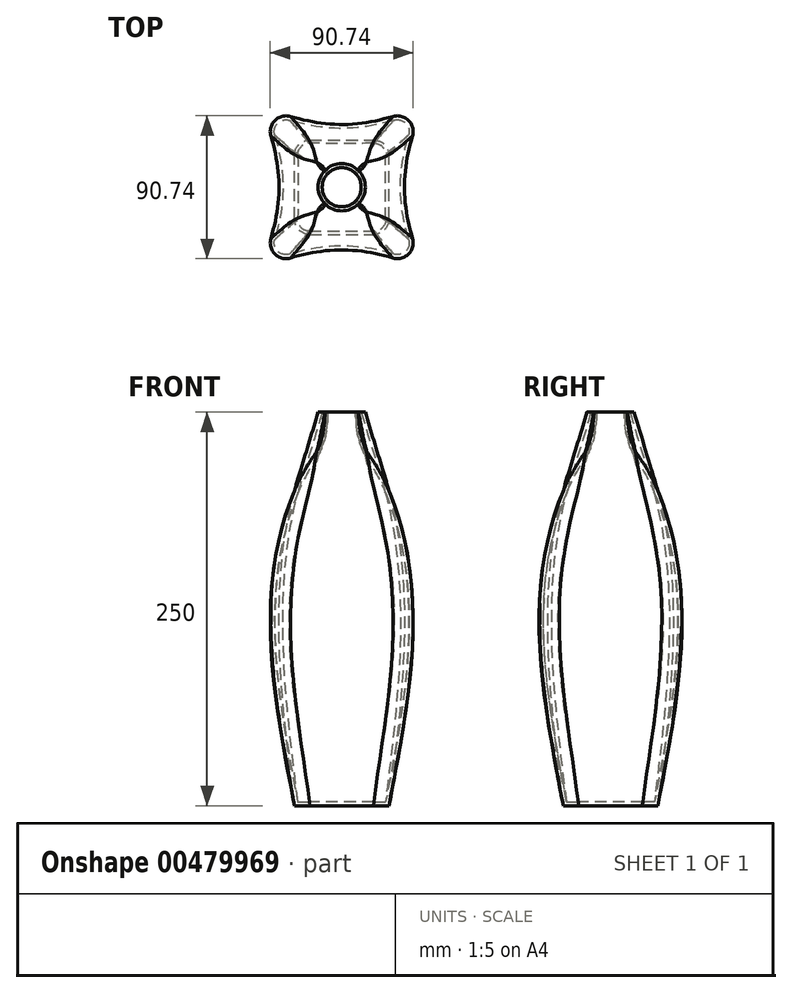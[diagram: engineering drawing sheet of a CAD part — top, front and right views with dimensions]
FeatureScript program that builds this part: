
annotation { "Feature Type Name" : "Feature", "Feature Type Description" : "" }
export const myFeature = defineFeature(function(context is Context, id is Id, definition is map)
    precondition{}
    {
        {
            var Q0;
            Q0=qCreatedBy(makeId("Top.planeOp"),FACE);
            var sketch = newSketch(context, id + "F0", { "sketchPlane" : qUnion([Q0])});
            skLineSegment(sketch, "E0.bottom", {"start": v(-30, -30) * mm, "end": v(30, -30) * mm});
            skLineSegment(sketch, "E0.top", {"start": v(-30, 30) * mm, "end": v(30, 30) * mm});
            skLineSegment(sketch, "E0.left", {"start": v(-30, -30) * mm, "end": v(-30, 30) * mm});
            skLineSegment(sketch, "E0.right", {"start": v(30, -30) * mm, "end": v(30, 30) * mm});
            skPoint(sketch, "E0.middle", {"position": v(0, 0) * mm});
            skSolve(sketch);
        }
        {
            var Q0;
            Q0=makeQuery(id+"F0.imprint","IMPRINT",FACE,{"disambiguationData":[TD([[makeQuery(id+"F0.imprint","IMPRINT",EDGE,{"derivedFrom":sQuery(id+"F0.wireOp",EDGE,"E0.bottom")}),1.0]])]});
            cPlane(context, id + "F1", {"entities" : qUnion([Q0]), "cplaneType" : CPlaneType.OFFSET, "offset" : 200 * mm, "width" : 150 * mm, "height" : 150 * mm});
        }
        {
            var Q0;
            Q0=qCreatedBy(id+"F1.planeOp",FACE);
            var sketch = newSketch(context, id + "F2", { "sketchPlane" : qUnion([Q0])});
            skLineSegment(sketch, "E1.bottom", {"start": v(30, -30) * mm, "end": v(-30, -30) * mm});
            skLineSegment(sketch, "E1.top", {"start": v(30, 30) * mm, "end": v(-30, 30) * mm});
            skLineSegment(sketch, "E1.left", {"start": v(30, -30) * mm, "end": v(30, 30) * mm});
            skLineSegment(sketch, "E1.right", {"start": v(-30, -30) * mm, "end": v(-30, 30) * mm});
            skPoint(sketch, "E1.middle", {"position": v(0, 0) * mm});
            skSolve(sketch);
        }
        {
            var Q0;
            Q0=qCreatedBy(id+"F1.planeOp",FACE);
            cPlane(context, id + "F3", {"entities" : qUnion([Q0]), "cplaneType" : CPlaneType.OFFSET, "offset" : 25 * mm, "width" : 150 * mm, "height" : 150 * mm});
        }
        {
            var Q0;
            Q0=qCreatedBy(id+"F3.planeOp",FACE);
            var sketch = newSketch(context, id + "F4", { "sketchPlane" : qUnion([Q0])});
            skPoint(sketch, "E2.middle", {"position": v(0, 0) * mm});
            skPoint(sketch, "E2.right.end.orphan", {"position": v(-32.39, 32.39) * mm});
            skPoint(sketch, "E2.bottom.end.orphan", {"position": v(-32.39, -32.39) * mm});
            skPoint(sketch, "E2.left.end.orphan", {"position": v(32.39, 32.39) * mm});
            skPoint(sketch, "E2.left.start.orphan", {"position": v(32.39, -32.39) * mm});
            skCircle(sketch, "E3", {"center": v(0, 0) * mm, "radius": 22.5 * mm});
            skSolve(sketch);
        }
        {
            var Q0;
            Q0=qCreatedBy(id+"F3.planeOp",FACE);
            cPlane(context, id + "F5", {"entities" : qUnion([Q0]), "cplaneType" : CPlaneType.OFFSET, "offset" : 25 * mm, "width" : 150 * mm, "height" : 150 * mm});
        }
        {
            var Q0;
            Q0=qCreatedBy(id+"F5.planeOp",FACE);
            var sketch = newSketch(context, id + "F6", { "sketchPlane" : qUnion([Q0])});
            skCircle(sketch, "E4", {"center": v(0, 0) * mm, "radius": 15 * mm});
            skSolve(sketch);
        }
        {
            var Q0;
            Q0=makeQuery(id+"F0.imprint","IMPRINT",FACE,{"disambiguationData":[TD([[makeQuery(id+"F0.imprint","IMPRINT",EDGE,{"derivedFrom":sQuery(id+"F0.wireOp",EDGE,"E0.bottom")}),1.0]])]});
            var Q1;
            Q1=makeQuery(id+"F2.imprint","IMPRINT",FACE,{"disambiguationData":[TD([[makeQuery(id+"F2.imprint","IMPRINT",EDGE,{"derivedFrom":sQuery(id+"F2.wireOp",EDGE,"E1.bottom")}),-1.0]])]});
            var Q2;
            Q2=makeQuery(id+"F4.imprint","IMPRINT",FACE,{"disambiguationData":[TD([[makeQuery(id+"F4.imprint","IMPRINT",EDGE,{"derivedFrom":sQuery(id+"F4.wireOp",EDGE,"E3")}),1.0]])]});
            var Q3;
            Q3=makeQuery(id+"F6.imprint","IMPRINT",FACE,{"disambiguationData":[TD([[makeQuery(id+"F6.imprint","IMPRINT",EDGE,{"derivedFrom":sQuery(id+"F6.wireOp",EDGE,"E4")}),1.0]])]});
            loft(context, id + "F7", {"sheetProfilesArray" : [{ "sheetProfileEntities" : qUnion([Q0]) }, { "sheetProfileEntities" : qUnion([Q1]) }, { "sheetProfileEntities" : qUnion([Q2]) }, { "sheetProfileEntities" : qUnion([Q3]) }]});
        }
        {
            var Q0;
            Q0=makeQuery(id+"F7.opLoft","SWEPT_EDGE",EDGE,{"disambiguationData":[OSD([sQuery(id+"F0.wireOp",EDGE,"E0.bottom"),sQuery(id+"F0.wireOp",EDGE,"E0.left"),sQuery(id+"F2.wireOp",EDGE,"E1.bottom"),sQuery(id+"F2.wireOp",EDGE,"E1.right")])]});
            var Q1;
            Q1=makeQuery(id+"F7.opLoft","SWEPT_EDGE",EDGE,{"disambiguationData":[OSD([sQuery(id+"F0.wireOp",EDGE,"E0.top"),sQuery(id+"F0.wireOp",EDGE,"E0.left"),sQuery(id+"F2.wireOp",EDGE,"E1.top"),sQuery(id+"F2.wireOp",EDGE,"E1.right")])]});
            var Q2;
            Q2=makeQuery(id+"F7.opLoft","SWEPT_EDGE",EDGE,{"disambiguationData":[OSD([sQuery(id+"F0.wireOp",EDGE,"E0.top"),sQuery(id+"F0.wireOp",EDGE,"E0.right"),sQuery(id+"F2.wireOp",EDGE,"E1.top"),sQuery(id+"F2.wireOp",EDGE,"E1.left")])]});
            var Q3;
            Q3=makeQuery(id+"F7.opLoft","SWEPT_EDGE",EDGE,{"disambiguationData":[OSD([sQuery(id+"F0.wireOp",EDGE,"E0.bottom"),sQuery(id+"F0.wireOp",EDGE,"E0.right"),sQuery(id+"F2.wireOp",EDGE,"E1.bottom"),sQuery(id+"F2.wireOp",EDGE,"E1.left")])]});
            fillet(context, id + "F8", {"entities" : qUnion([Q0, Q1, Q2, Q3]), "radius" : 10 * mm, "tangentPropagation" : true, "allowEdgeOverflow" : false});
        }
        {
            var Q0;
            Q0=makeQuery(id+"F7.opLoft","CAP_FACE",FACE,{"disambiguationData":[OSD([makeQuery(id+"F6.imprint","IMPRINT",FACE,{"disambiguationData":[TD([[makeQuery(id+"F6.imprint","IMPRINT",EDGE,{"derivedFrom":sQuery(id+"F6.wireOp",EDGE,"E4")}),1.0]])]})])],"isStart":true});
            shell(context, id + "F9", {"entities" : qUnion([Q0]), "thickness" : 2.5 * mm});
        }
    });
